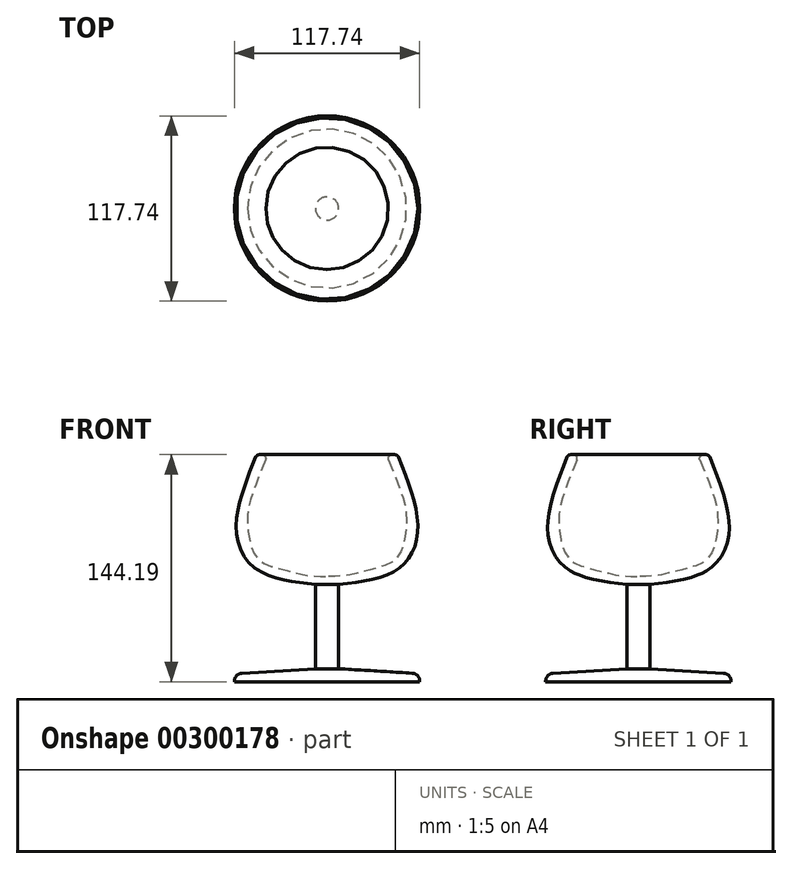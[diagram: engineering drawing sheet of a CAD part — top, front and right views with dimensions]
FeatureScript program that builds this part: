
annotation { "Feature Type Name" : "Feature", "Feature Type Description" : "" }
export const myFeature = defineFeature(function(context is Context, id is Id, definition is map)
    precondition{}
    {
        {
            var Q0;
            Q0=qCreatedBy(makeId("Front.planeOp"),FACE);
            var sketch = newSketch(context, id + "F0", { "sketchPlane" : qUnion([Q0])});
            skLineSegment(sketch, "E0", {"start": v(0, -76.71) * mm, "end": v(-58.87, -76.71) * mm});
            skLineSegment(sketch, "E1", {"start": v(-58.87, -76.71) * mm, "end": v(-58.87, -71.6) * mm});
            skLineSegment(sketch, "E2", {"start": v(-58.87, -71.6) * mm, "end": v(-7.4, -68.46) * mm});
            skLineSegment(sketch, "E3", {"start": v(-7.4, -68.46) * mm, "end": v(-7.4, -15.03) * mm});
            skLineSegment(sketch, "E4", {"start": v(0, -9.92) * mm, "end": v(0, -76.71) * mm, "construction": true});
            skFitSpline(sketch, "E5", {"points": [v(-7.4, -15.03) * mm, v(-45.51, -4.81) * mm, v(-57.7, 20.72) * mm, v(-44.73, 67.48) * mm], "startDerivative": vector(-127.87, 15.59) * mm, "endDerivative": vector(52.75, 131.17) * mm});
            skLineSegment(sketch, "E6", {"start": v(-44.73, 67.48) * mm, "end": v(-37.65, 67.48) * mm});
            skLineSegment(sketch, "E7", {"start": v(0, -9.92) * mm, "end": v(0, -76.71) * mm});
            skFitSpline(sketch, "E8", {"points": [v(-37.65, 67.48) * mm, v(-45.51, 47.83) * mm, v(-50.23, 30.55) * mm, v(-49.05, 12.47) * mm, v(-42.37, 0) * mm, v(-25.87, -6) * mm, v(-12.5, -9.14) * mm, v(0, -9.92) * mm], "startDerivative": vector(-50.61, -122.9) * mm, "endDerivative": vector(101, -1.88) * mm});
            skPoint(sketch, "E9.end.orphan", {"position": v(0, 67.48) * mm});
            skPoint(sketch, "E9.start.orphan", {"position": v(0, 75.34) * mm});
            skSolve(sketch);
        }
        {
            var Q0;
            Q0 = qSketchRegion(id + "F0", true);
            var Q1;
            Q1=sQuery(id+"F0.wireOp",EDGE,"E7");
            revolve(context, id + "F1", {"entities" : qUnion([Q0]), "axis" : qUnion([Q1]), "revolveType" : RevolveType.FULL});
        }
        {
            var Q0;
            Q0=makeQuery(id+"F1.opRevolve","SWEPT_EDGE",EDGE,{"disambiguationData":[OSD([sQuery(id+"F0.wireOp",EDGE,"E5"),sQuery(id+"F0.wireOp",EDGE,"E6")])]});
            var Q1;
            Q1=makeQuery(id+"F1.opRevolve","SWEPT_EDGE",EDGE,{"disambiguationData":[OSD([sQuery(id+"F0.wireOp",EDGE,"E6"),sQuery(id+"F0.wireOp",EDGE,"E8")])]});
            fillet(context, id + "F2", {"entities" : qUnion([Q0, Q1]), "radius" : 2.54 * mm, "tangentPropagation" : true, "allowEdgeOverflow" : false});
        }
        {
            var Q0;
            Q0=makeQuery(id+"F1.opRevolve","SWEPT_EDGE",EDGE,{"disambiguationData":[OSD([sQuery(id+"F0.wireOp",EDGE,"E1"),sQuery(id+"F0.wireOp",EDGE,"E2")])]});
            fillet(context, id + "F3", {"entities" : qUnion([Q0]), "radius" : 5.08 * mm, "tangentPropagation" : true, "allowEdgeOverflow" : false});
        }
    });
